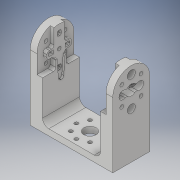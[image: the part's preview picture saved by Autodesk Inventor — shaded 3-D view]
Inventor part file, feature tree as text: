
AUTODESK INVENTOR PART (.ipt)
format: ipt  version: 2018 (Build 220112000, 112)  size: 655,360 bytes
history: native  units: in
note: dims shown in document units (in); Inventor stores cm internally (conversion verified against a paired STEP export)
features: extrude x15, sketch x15, fillet x9, mirror x8, plane x2
ambient origin geometry x8: Origin, YZ Plane, XZ Plane, XY Plane, X Axis, Y Axis, Z Axis, Center Point
bodies: Solid1 (feature_tree)
feature tree (49):
  extrude  "U_Profile"  Depth=1.8504in
  extrude  "Shaft_Opening"  Depth=1.1811in TaperAngle=0.0deg
  extrude  "Nut_Slot"  Depth=1.1811in
  extrude  "Docking_Holes_Front"  Depth=0.5906in
  extrude  "Servo_Horn_Slot"  Depth=0.1969in
  fillet  "Fillet4"  Radius=0.3937in
  fillet  "Fillet9"  Radius=0.2165in
  extrude  "Docking_Holes_Lateral"  Depth=1.1811in
  plane  "Work Plane6"
  mirror  "Mirror7"
  extrude  "Cable_Opening_Front"  Depth=0.5906in
  extrude  "Openings_ServoHorn_Fixation"  Depth=0.1181in
  mirror  "Mirror8"
  fillet  "Fillet11"  Radius=0.1181in
  extrude  "Nut_Slot_Docking_Lateral_01"  TaperAngle=45.0deg  [1 undecoded]
  extrude  "Nut_Slot_Docking_Lateral_02"  Depth=0.1181in
  mirror  "Mirror10"
  extrude  "Servo_Screws_Slots"  Depth=0.1181in
  mirror  "Mirror11"
  fillet  "Fillet12"  Radius=0.1181in
  mirror  "Mirror12"
  fillet  "Fillet13"  Radius=0.1181in
  fillet  "Fillet14"  Radius=0.1181in
  extrude  "Extrusion21"  Depth=0.1575in
  fillet  "Fillet16"  Radius=0.748in
  extrude  "Material_Reduction_01"  Depth=0.2165in
  extrude  "Servo_Horn_Opening"  Depth=0.1575in
  mirror  "Mirror13"
  extrude  "Material_Reduction_02"  Depth=0.1378in
  fillet  "Fillet17"  Radius=0.0591in
  plane  "Work Plane8"
  mirror  "Mirror14"
  mirror  "Mirror15"
  fillet  "Fillet18"  Radius=0.0787in
  sketch  "Sketch1"  dims[d0=1.8504in d1=2.4803in]
  sketch  "Sketch2"  dims[d2=0.3937in d5=1.1811in d6=0.0in]
  sketch  "Sketch4"  dims[d7=0.1181in d8=1.1811in]
  sketch  "Sketch6"  dims[d9=0.5906in d10=0.685in]
  sketch  "Sketch8"  dims[d11=0.7874in d12=0.0in d13=0.1969in d18=0.3937in d19=0.2165in d20=0.0in]
  sketch  "Sketch11"  dims[d21=0.8661in d22=1.1811in]
  sketch  "Sketch12"  dims[d23=0.5906in d24=0.9252in]
  sketch  "Sketch13"  dims[d25=1.8504in d26=0.1181in d27=0.1181in]
  sketch  "Sketch15"  dims[d28=45.0deg d29=45.0deg]
  sketch  "Sketch16"  dims[d30=90.0deg d31=0.1181in]
  sketch  "Sketch17"  dims[d32=0.1181in d33=0.1181in d34=0.1181in d35=0.1181in d36=0.1181in]
  sketch  "Sketch22"  dims[d37=0.3937in d38=0.0in d48=0.1575in d52=0.748in]
  sketch  "Sketch23"  dims[d54=0.2165in d55=0.2165in]
  sketch  "Sketch24"  dims[d56=0.1575in d57=0.5118in]
  sketch  "Sketch25"  dims[d58=0.6299in d59=0.6299in d60=0.0591in d61=0.0in d63=0.0787in d64=0.3937in d97=0.5906in d98=0.8661in d99=45.0deg d100=45.0deg d101=0.1181in d102=0.1181in d103=0.1181in d104=0.1181in d105=0.3937in d106=0.0in d109=0.0787in d113=0.3937in d114=2.6378in d115=1.3189in d116=1.1811in d117=0.5906in d118=0.3937in d119=0.0in d120=0.1181in d121=0.1575in d122=1.1811in d123=0.5906in d124=0.6125in d125=0.3062in d127=0.5118in d128=0.1181in d131=0.1575in d132=0.1181in d133=0.1575in d134=0.4331in d135=0.1181in d136=0.1575in d138=0.1181in d139=0.0in d152=0.1969in d153=0.2756in d154=0.2756in d156=0.1772in d157=0.0in d160=0.1181in d161=0.0in d163=0.2559in d164=0.2559in d165=0.2559in d166=0.1181in d167=0.0591in d168=0.1181in d169=0.0591in d170=0.1575in d172=0.1575in d173=0.0787in d174=0.1575in d175=0.0787in d178=0.1969in d179=0.0in d180=0.0394in d183=0.0787in d189=0.1575in d190=0.4331in d192=0.2559in d199=0.3543in d200=0.1772in d201=0.3937in d202=0.1969in d205=0.1378in d208=0.1378in d209=0.0787in d210=0.1969in d211=0.1969in d212=0.0787in d221=0.0787in d228=0.3937in d229=0.6693in d230=0.5906in d231=1.1811in d232=0.5906in d233=0.3937in d234=0.0in d235=0.1181in d239=0.3937in d240=0.0in d241=0.0787in d242=0.3346in d243=1.1811in d244=0.5906in d245=0.0079in d246=0.3937in d247=0.0in d248=0.3937in d249=0.3937in d250=0.0in d251=0.0787in d252=0.3937in d253=0.0787in d254=0.1575in d255=0.0787in d256=0.5906in d257=0.1378in]
note: 1 required parameter value undecoded (feature->parameter linkage not recoverable at this tier; creation-order binding heuristic only, values carry confidence <= 0.55)
